FCSTD DOCUMENT  (FreeCAD 0.21R33771 (Git))
Label: ConsoleKeyStickers
License: All rights reserved
LicenseURL: http://en.wikipedia.org/wiki/All_rights_reserved
objects: Sketcher::SketchObject×1, PartDesign::Body×1
note: 2 computed .brp shape members not serialized (recipe doc carries the construction recipe); baked Part::Feature solids carry a one-line shape summary decoded from their .brp

FEATURE [Sketcher::SketchObject] Sketch
  FullyConstrained = true
  MapMode = 5
  Support = -> [XY_Plane]
  expr: Constraints[21] = (26.4 * cos(45) - 5) / cos(45)
  sketch-geometry (16):
    g0: LineSegment StartX=0 StartY=-3.6e-15 StartZ=0 EndX=13.6676 EndY=13.6676 EndZ=0
    g1: LineSegment StartX=13.6676 StartY=13.6676 StartZ=0 EndX=40.0676 EndY=13.6676 EndZ=0
    g2: LineSegment StartX=40.0676 StartY=13.6676 StartZ=0 EndX=26.4 EndY=-3.6e-15 EndZ=0
    g3: LineSegment StartX=21.63 StartY=-11.36 StartZ=0 EndX=21.63 EndY=-15.36 EndZ=0
    g4: LineSegment StartX=21.63 StartY=-15.36 StartZ=0 EndX=-4.77 EndY=-15.36 EndZ=0
    g5: LineSegment StartX=-4.77 StartY=-15.36 StartZ=0 EndX=-4.77 EndY=-11.36 EndZ=0
    g6: ArcOfEllipse CenterX=38.9016 CenterY=-11.36 CenterZ=0 NormalX=0 NormalY=0 NormalZ=1 MajorRadius=17.2716 MinorRadius=16.4641 AngleXU=-3.14159 StartAngle=5.52172 EndAngle=6.28319
    g7: LineSegment StartX=21.63 StartY=-11.36 StartZ=0 EndX=56.1732 EndY=-11.36 EndZ=0
    g8: LineSegment StartX=38.9016 StartY=-27.8241 StartZ=0 EndX=38.9016 EndY=5.10413 EndZ=0
    g9: GeomPoint X=33.6824 Y=-11.36 Z=0
    g10: GeomPoint X=44.1208 Y=-11.36 Z=0
    g11: ArcOfEllipse CenterX=12.5016 CenterY=-11.36 CenterZ=0 NormalX=0 NormalY=0 NormalZ=1 MajorRadius=17.2716 MinorRadius=16.4641 AngleXU=-3.14159 StartAngle=5.52172 EndAngle=6.28319
    g12: LineSegment StartX=-4.77 StartY=-11.36 StartZ=0 EndX=29.7732 EndY=-11.36 EndZ=0
    g13: LineSegment StartX=12.5016 StartY=-27.8241 StartZ=0 EndX=12.5016 EndY=5.10413 EndZ=0
    g14: GeomPoint X=7.28238 Y=-11.36 Z=0
    g15: GeomPoint X=17.7208 Y=-11.36 Z=0
  constraints (29):
    c: Coincident(g-1,g0)
    c: Coincident(g0,g1)
    c: Horizontal(g1)
    c: Coincident(g1,g2)
    c: PointOnObject(g2,g-1)
    c: Vertical(g3)
    c: Coincident(g3,g4)
    c: Horizontal(g4)
    c: Coincident(g4,g5)
    c: Vertical(g5)
    c: Angle(g-1,g0) = 0.785398
    c: Parallel(g0,g2)
    c: DistanceX(g1,g1) = 26.4
    c: InternalAlignment(g7-g10 -> g6) x4
    c: Tangent(g6,g2) = -1.5708
    c: Tangent(g6,g3) = -1.5708
    c: Horizontal(g7)
    c: Horizontal(g5,g3)
    c: Distance(g2) = 19.3289
    c: DistanceY(g5,g5) = 4
    c: Equal(g4,g1)
    c: DistanceY(g3,g2) = 11.36
    c: DistanceX(g3,g2) = 4.77
    c: InternalAlignment(g12-g15 -> g11) x4
    c: Coincident(g11,g0)
    c: Coincident(g11,g5)
    c: Horizontal(g12,g7)
    c: Vertical(g13,g11)
    c: Horizontal(g13,g8)
FEATURE [PartDesign::Body] Body
  Group = -> [Sketch]
  Origin = -> Origin
